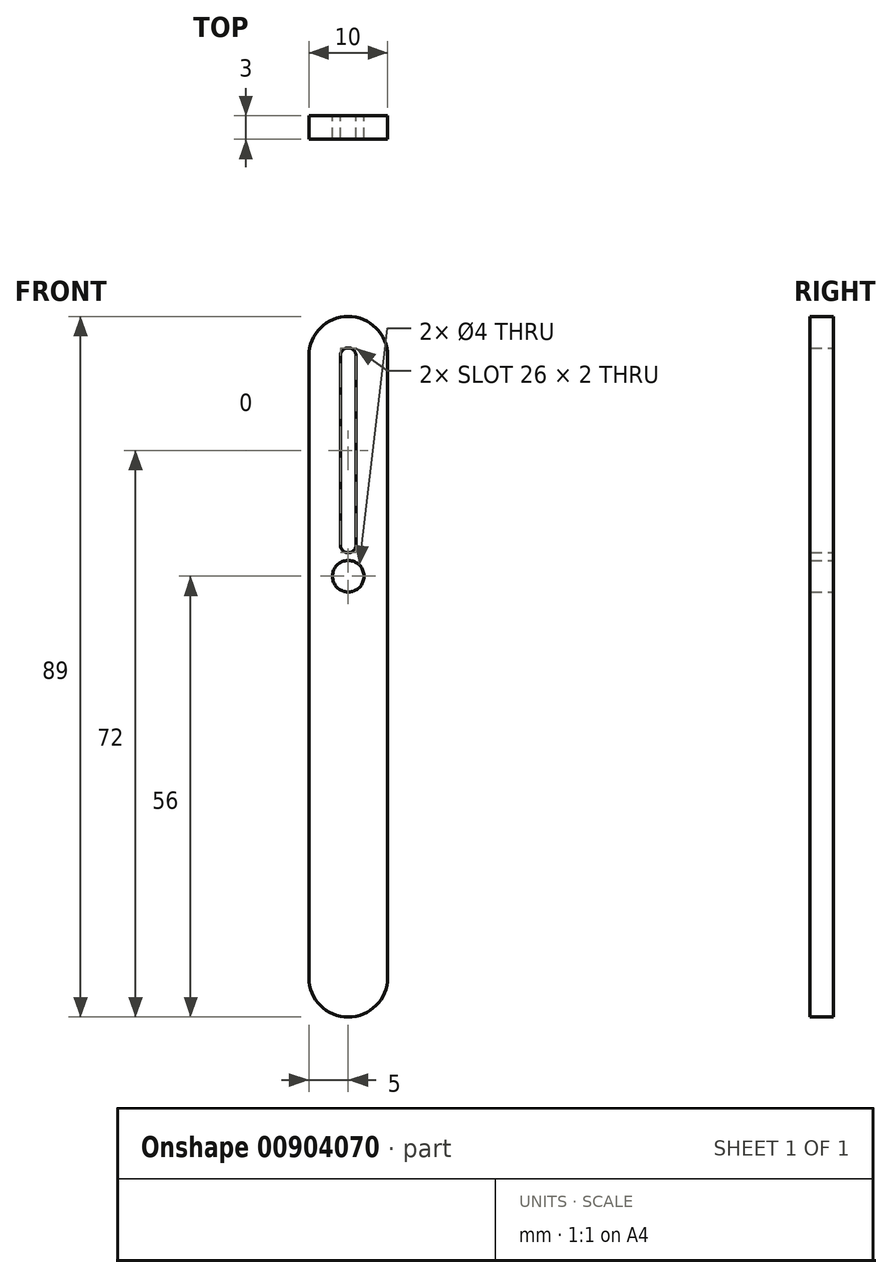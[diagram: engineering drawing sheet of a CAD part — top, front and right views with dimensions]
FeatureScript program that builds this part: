
annotation { "Feature Type Name" : "Feature", "Feature Type Description" : "" }
export const myFeature = defineFeature(function(context is Context, id is Id, definition is map)
    precondition{}
    {
        {
            var Q0;
            Q0=qCreatedBy(makeId("Front.planeOp"),FACE);
            var sketch = newSketch(context, id + "F0", { "sketchPlane" : qUnion([Q0])});
            skArc(sketch, "E0", {"start": v(-5, 0) * mm, "mid": v(0, -5) * mm, "end": v(5, 0) * mm});
            skArc(sketch, "E1", {"start": v(5, 79) * mm, "mid": v(0, 84) * mm, "end": v(-5, 79) * mm});
            skLineSegment(sketch, "E2", {"start": v(-5, 79) * mm, "end": v(-5, 0) * mm});
            skLineSegment(sketch, "E3.MirrorCS", {"start": v(5, 79) * mm, "end": v(5, 0) * mm});
            skArc(sketch, "E4", {"start": v(1, 79) * mm, "mid": v(0, 80) * mm, "end": v(-1, 79) * mm});
            skArc(sketch, "E5", {"start": v(-1, 55) * mm, "mid": v(0, 54) * mm, "end": v(1, 55) * mm});
            skCircle(sketch, "E6", {"center": v(0, 51) * mm, "radius": 2 * mm});
            skLineSegment(sketch, "E7", {"start": v(-1, 79) * mm, "end": v(-1, 55) * mm});
            skLineSegment(sketch, "E8", {"start": v(1, 79) * mm, "end": v(1, 55) * mm});
            skSolve(sketch);
        }
        {
            var Q0;
            Q0 = qSketchRegion(id + "F0", true);
            extrude(context, id + "F1", {"entities" : qUnion([Q0]), "depth" : 3 * mm, "offsetDistance" : 25 * mm});
        }
    });
